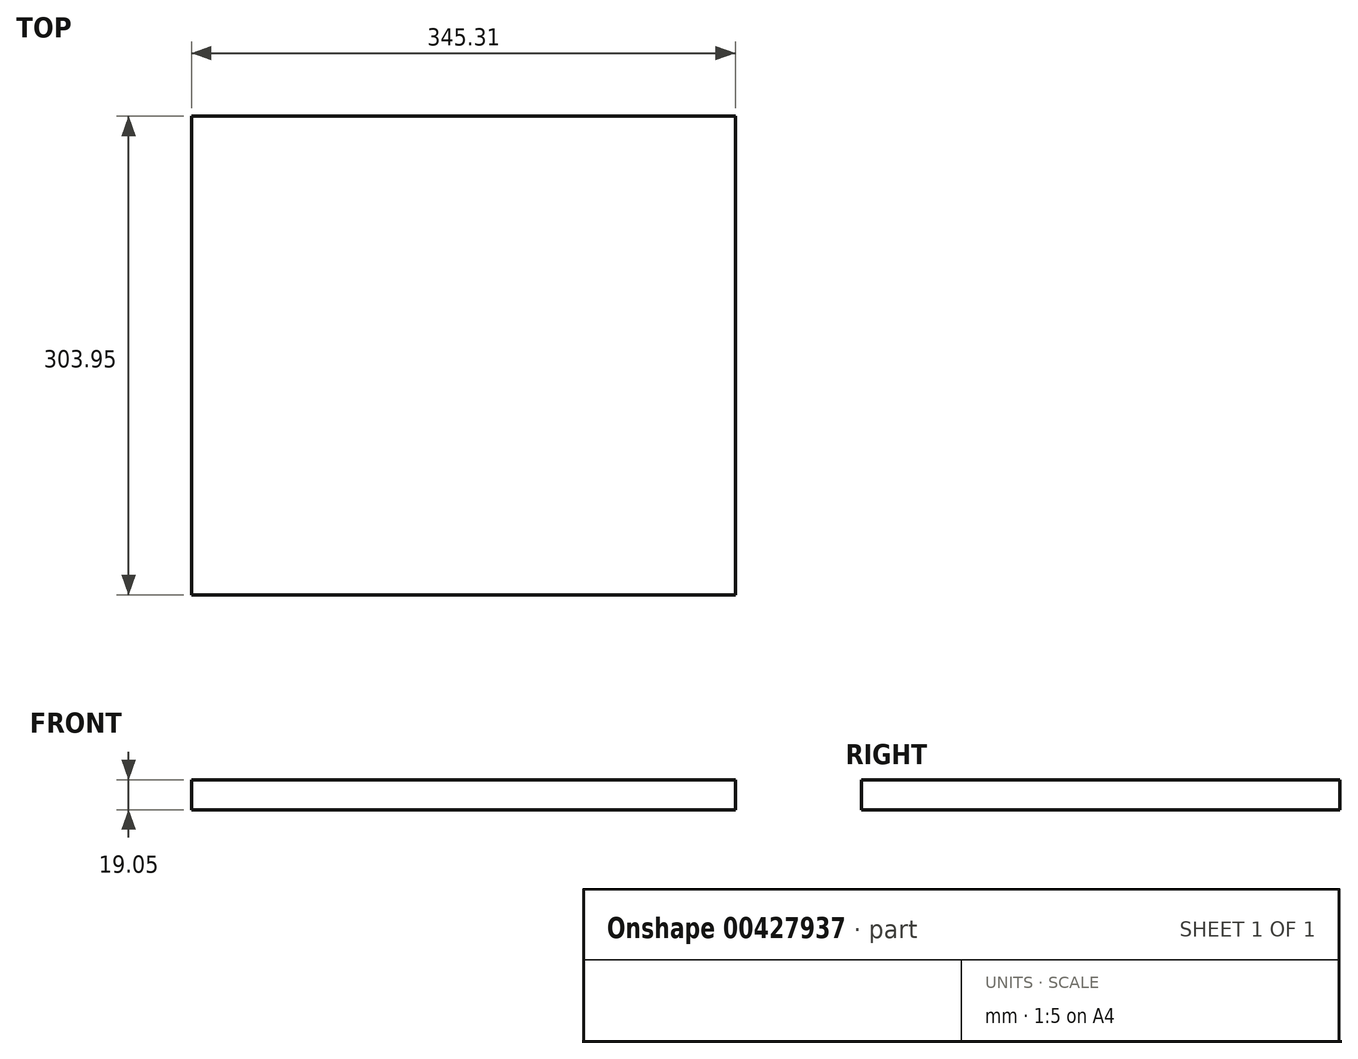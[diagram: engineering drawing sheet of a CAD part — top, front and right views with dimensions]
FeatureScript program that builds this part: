
annotation { "Feature Type Name" : "Feature", "Feature Type Description" : "" }
export const myFeature = defineFeature(function(context is Context, id is Id, definition is map)
    precondition{}
    {
        {
            var Q0;
            Q0=qCreatedBy(makeId("Top.planeOp"),FACE);
            var sketch = newSketch(context, id + "F0", { "sketchPlane" : qUnion([Q0])});
            skLineSegment(sketch, "E0.bottom", {"start": v(-78.53, 74.51) * mm, "end": v(266.78, 74.51) * mm});
            skLineSegment(sketch, "E0.top", {"start": v(-78.53, -229.44) * mm, "end": v(266.78, -229.44) * mm});
            skLineSegment(sketch, "E0.left", {"start": v(-78.53, 74.51) * mm, "end": v(-78.53, -229.44) * mm});
            skLineSegment(sketch, "E0.right", {"start": v(266.78, 74.51) * mm, "end": v(266.78, -229.44) * mm});
            skSolve(sketch);
        }
        {
            var Q0;
            Q0=makeQuery(id+"F0.imprint","IMPRINT",FACE,{"disambiguationData":[TD([[makeQuery(id+"F0.imprint","IMPRINT",EDGE,{"derivedFrom":sQuery(id+"F0.wireOp",EDGE,"E0.bottom")}),-1.0]])]});
            extrude(context, id + "F1", {"entities" : qUnion([Q0]), "depth" : 19.05 * mm});
        }
    });
